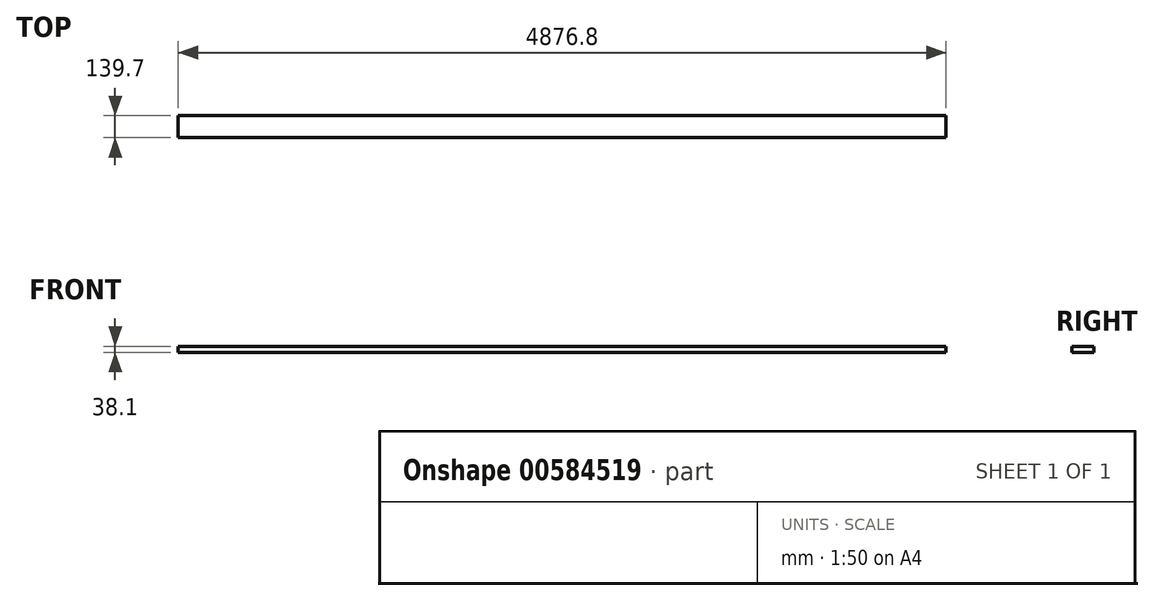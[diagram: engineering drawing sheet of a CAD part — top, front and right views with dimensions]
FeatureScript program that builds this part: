
annotation { "Feature Type Name" : "Feature", "Feature Type Description" : "" }
export const myFeature = defineFeature(function(context is Context, id is Id, definition is map)
    precondition{}
    {
        {
            var Q0;
            Q0=qCreatedBy(makeId("Top.planeOp"), FACE);
            var sketch = newSketch(context, id + "F0", { "sketchPlane" : qUnion([Q0])});
            skLineSegment(sketch, "E0.bottom", {"start": v(0, 0) * mm, "end": v(4876.8, 0) * mm});
            skLineSegment(sketch, "E0.top", {"start": v(0, 139.7) * mm, "end": v(4876.8, 139.7) * mm});
            skLineSegment(sketch, "E0.left", {"start": v(0, 0) * mm, "end": v(0, 139.7) * mm});
            skLineSegment(sketch, "E0.right", {"start": v(4876.8, 0) * mm, "end": v(4876.8, 139.7) * mm});
            skSolve(sketch);
        }
        {
            var Q0;
            Q0 = qSketchRegion(id + "F0", true);
            extrude(context, id + "F1", {"entities" : qUnion([Q0]), "depth" : 38.1 * mm, "offsetDistance" : 25.4 * mm});
        }
    });
